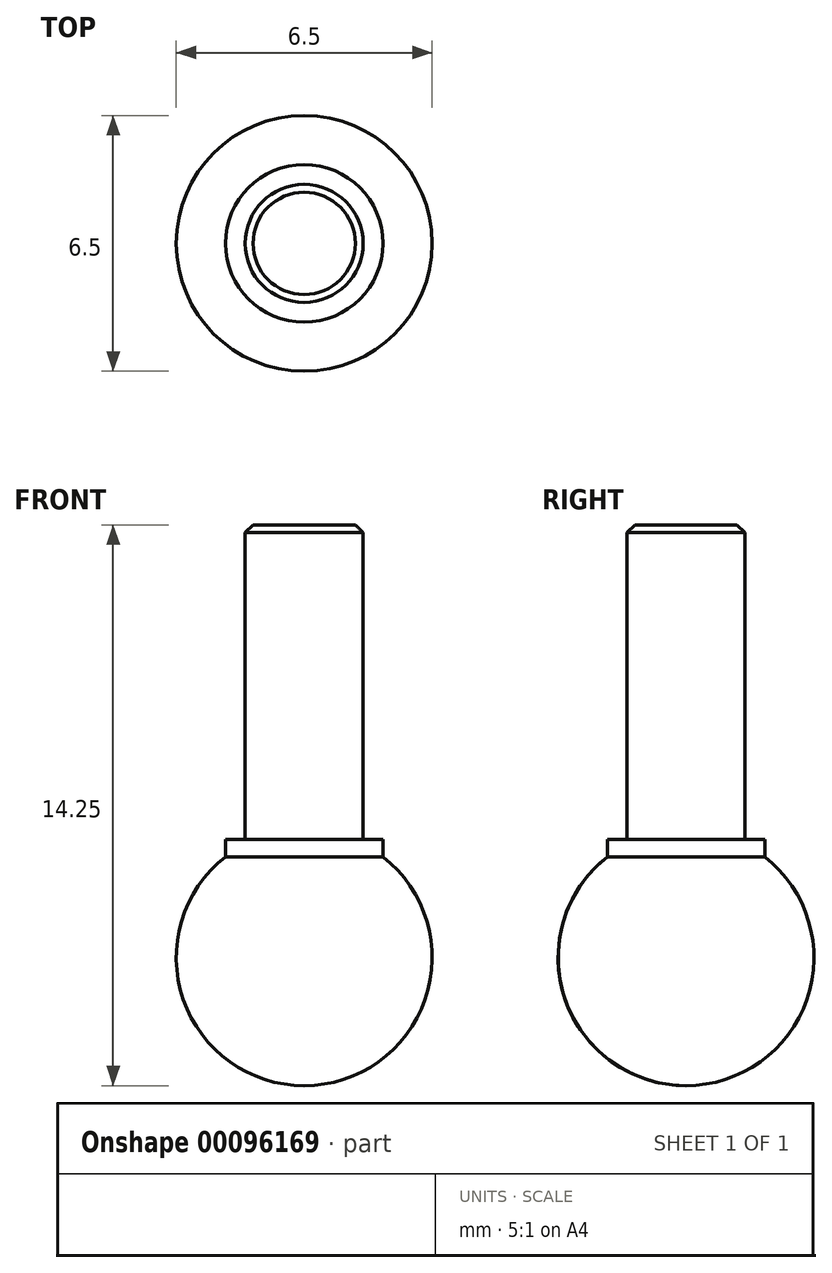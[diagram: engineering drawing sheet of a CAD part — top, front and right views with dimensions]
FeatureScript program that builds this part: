
annotation { "Feature Type Name" : "Feature", "Feature Type Description" : "" }
export const myFeature = defineFeature(function(context is Context, id is Id, definition is map)
    precondition{}
    {
        {
            var Q0;
            Q0=qCreatedBy(makeId("Right.planeOp"),FACE);
            var sketch = newSketch(context, id + "F0", { "sketchPlane" : qUnion([Q0])});
            skArc(sketch, "E0", {"start": v(0, -3.25) * mm, "mid": v(3.25, 0) * mm, "end": v(0, 3.25) * mm});
            skLineSegment(sketch, "E1", {"start": v(0, 3.25) * mm, "end": v(0, -3.25) * mm});
            skSolve(sketch);
        }
        {
            var Q0;
            Q0 = qSketchRegion(id + "F0", true);
            var Q1;
            Q1=sQuery(id+"F0.wireOp",EDGE,"E1");
            revolve(context, id + "F1", {"entities" : qUnion([Q0]), "axis" : qUnion([Q1]), "revolveType" : RevolveType.FULL});
        }
        {
            var Q0;
            Q0=qCreatedBy(makeId("Top.planeOp"),FACE);
            var sketch = newSketch(context, id + "F2", { "sketchPlane" : qUnion([Q0])});
            skCircle(sketch, "E2", {"center": v(0, 0) * mm, "radius": 2 * mm});
            skSolve(sketch);
        }
        {
            var Q0;
            Q0 = qSketchRegion(id + "F2", true);
            extrude(context, id + "F3", {"entities" : qUnion([Q0]), "operationType" : NewBodyOperationType.ADD, "depth" : 3 * mm});
        }
        {
            var Q0;
            Q0=makeQuery(id+"F3.opExtrude","CAP_FACE",FACE,{"disambiguationData":[OSD([sQuery(id+"F2.wireOp",EDGE,"E2")])],"isStart":false});
            var sketch = newSketch(context, id + "F4", { "sketchPlane" : qUnion([Q0])});
            skCircle(sketch, "E3", {"center": v(0, 0) * mm, "radius": 1.5 * mm});
            skSolve(sketch);
        }
        {
            var Q0;
            Q0 = qSketchRegion(id + "F4", true);
            extrude(context, id + "F5", {"entities" : qUnion([Q0]), "operationType" : NewBodyOperationType.ADD, "depth" : 8 * mm});
        }
        {
            var Q0;
            Q0=makeQuery(id+"F5.opExtrude","CAP_EDGE",EDGE,{"disambiguationData":[OSD([sQuery(id+"F4.wireOp",EDGE,"E3")])],"isStart":false});
            chamfer(context, id + "F6", {"entities" : qUnion([Q0]), "width" : .2 * mm, "tangentPropagation" : true});
        }
    });
